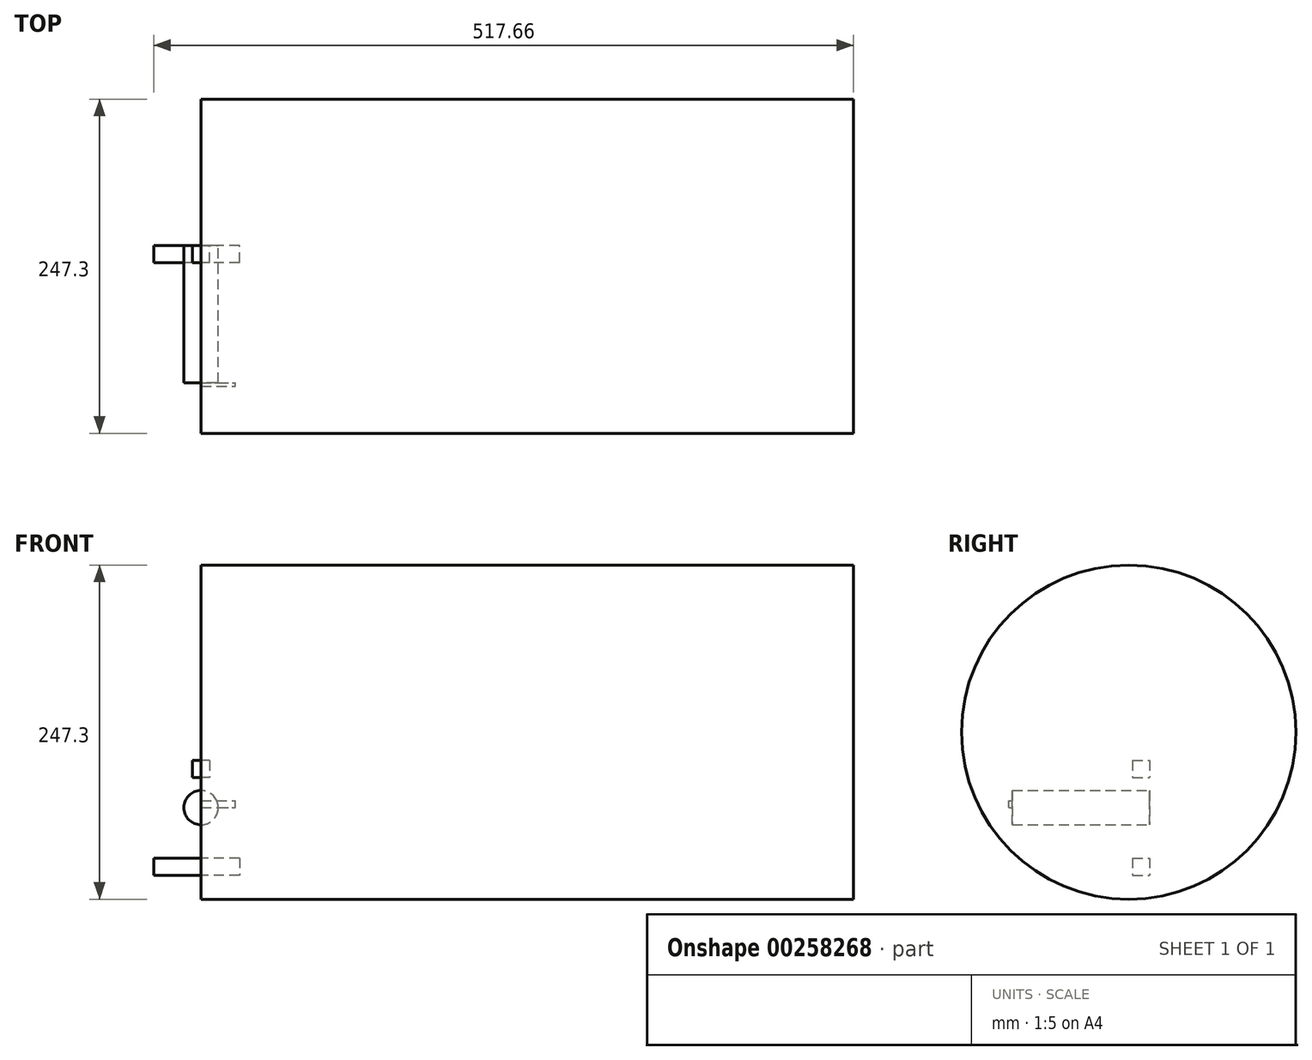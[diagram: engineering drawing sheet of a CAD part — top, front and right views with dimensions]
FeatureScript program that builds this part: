
annotation { "Feature Type Name" : "Feature", "Feature Type Description" : "" }
export const myFeature = defineFeature(function(context is Context, id is Id, definition is map)
    precondition{}
    {
        {
            var Q0;
            Q0=qCreatedBy(makeId("Front.planeOp"),FACE);
            var sketch = newSketch(context, id + "F0", { "sketchPlane" : qUnion([Q0])});
            skCircle(sketch, "E0", {"center": v(0, 0) * mm, "radius": 12.7 * mm});
            skSolve(sketch);
        }
        {
            var Q0;
            Q0=qSketchRegion(id+"F0",true);
            extrude(context, id + "F1", {"entities" : qUnion([Q0]), "depth" : 101.6 * mm});
        }
        {
            var Q0;
            Q0=qCreatedBy(makeId("Front.planeOp"),FACE);
            var sketch = newSketch(context, id + "F2", { "sketchPlane" : qUnion([Q0])});
            skLineSegment(sketch, "E1.bottom", {"start": v(28.44, -37.26) * mm, "end": v(-35.06, -37.26) * mm});
            skLineSegment(sketch, "E1.top", {"start": v(28.44, -49.96) * mm, "end": v(-35.06, -49.96) * mm});
            skLineSegment(sketch, "E1.left", {"start": v(28.44, -37.26) * mm, "end": v(28.44, -49.96) * mm});
            skLineSegment(sketch, "E1.right", {"start": v(-35.06, -37.26) * mm, "end": v(-35.06, -49.96) * mm});
            skSolve(sketch);
        }
        {
            var Q0;
            Q0=qSketchRegion(id+"F2",true);
            extrude(context, id + "F3", {"entities" : qUnion([Q0]), "depth" : 12.7 * mm});
        }
        {
            var Q0;
            Q0=makeQuery(id+"F1.opExtrude","CAP_FACE",FACE,{"disambiguationData":[OSD([sQuery(id+"F0.wireOp",EDGE,"E0")])],"isStart":false});
            var sketch = newSketch(context, id + "F4", { "sketchPlane" : qUnion([Q0])});
            skLineSegment(sketch, "E2.bottom", {"start": v(0, 0) * mm, "end": v(25.4, 0) * mm});
            skLineSegment(sketch, "E2.top", {"start": v(0, 5.08) * mm, "end": v(25.4, 5.08) * mm});
            skLineSegment(sketch, "E2.left", {"start": v(0, 0) * mm, "end": v(0, 5.08) * mm});
            skLineSegment(sketch, "E2.right", {"start": v(25.4, 0) * mm, "end": v(25.4, 5.08) * mm});
            skSolve(sketch);
        }
        {
            var Q0;
            {var subQ0=sQuery(id+"F4.wireOp",EDGE,"E2.right");Q0=makeQuery(id+"F4.imprint","IMPRINT",FACE,{"disambiguationData":[TD([[makeQuery(id+"F4.imprint","IMPRINT",EDGE,{"derivedFrom":subQ0}),1.0]])]});}
            var Q1;
            {var subQ0=sQuery(id+"F4.wireOp",EDGE,"E2.left");Q1=makeQuery(id+"F4.imprint","IMPRINT",FACE,{"disambiguationData":[TD([[makeQuery(id+"F4.imprint","IMPRINT",EDGE,{"derivedFrom":subQ0}),-1.0]])]});}
            extrude(context, id + "F5", {"entities" : qUnion([Q0, Q1]), "operationType" : NewBodyOperationType.ADD, "depth" : 2.54 * mm});
        }
        {
            var Q0;
            Q0=qCreatedBy(makeId("Front.planeOp"),FACE);
            var sketch = newSketch(context, id + "F6", { "sketchPlane" : qUnion([Q0])});
            skLineSegment(sketch, "E3.bottom", {"start": v(6.35, 34.92) * mm, "end": v(-6.35, 34.92) * mm});
            skLineSegment(sketch, "E3.top", {"start": v(6.35, 22.22) * mm, "end": v(-6.35, 22.22) * mm});
            skLineSegment(sketch, "E3.left", {"start": v(6.35, 34.92) * mm, "end": v(6.35, 22.22) * mm});
            skLineSegment(sketch, "E3.right", {"start": v(-6.35, 34.92) * mm, "end": v(-6.35, 22.22) * mm});
            skPoint(sketch, "E3.middle", {"position": v(0, 28.57) * mm});
            skSolve(sketch);
        }
        {
            var Q0;
            Q0=qSketchRegion(id+"F6",true);
            extrude(context, id + "F7", {"entities" : qUnion([Q0]), "depth" : 12.7 * mm});
        }
        {
            var Q0;
            Q0=qCreatedBy(makeId("Right.planeOp"),FACE);
            var sketch = newSketch(context, id + "F8", { "sketchPlane" : qUnion([Q0])});
            skCircle(sketch, "E4", {"center": v(-15.44, 55.93) * mm, "radius": 123.65 * mm});
            skSolve(sketch);
        }
        {
            var Q0;
            Q0=makeQuery(id+"F8.imprint","IMPRINT",FACE,{"disambiguationData":[TD([[makeQuery(id+"F8.imprint","IMPRINT",EDGE,{"derivedFrom":sQuery(id+"F8.wireOp",EDGE,"E4")}),1.0]])]});
            extrude(context, id + "F9", {"entities" : qUnion([Q0]), "depth" : 482.6 * mm});
        }
    });
